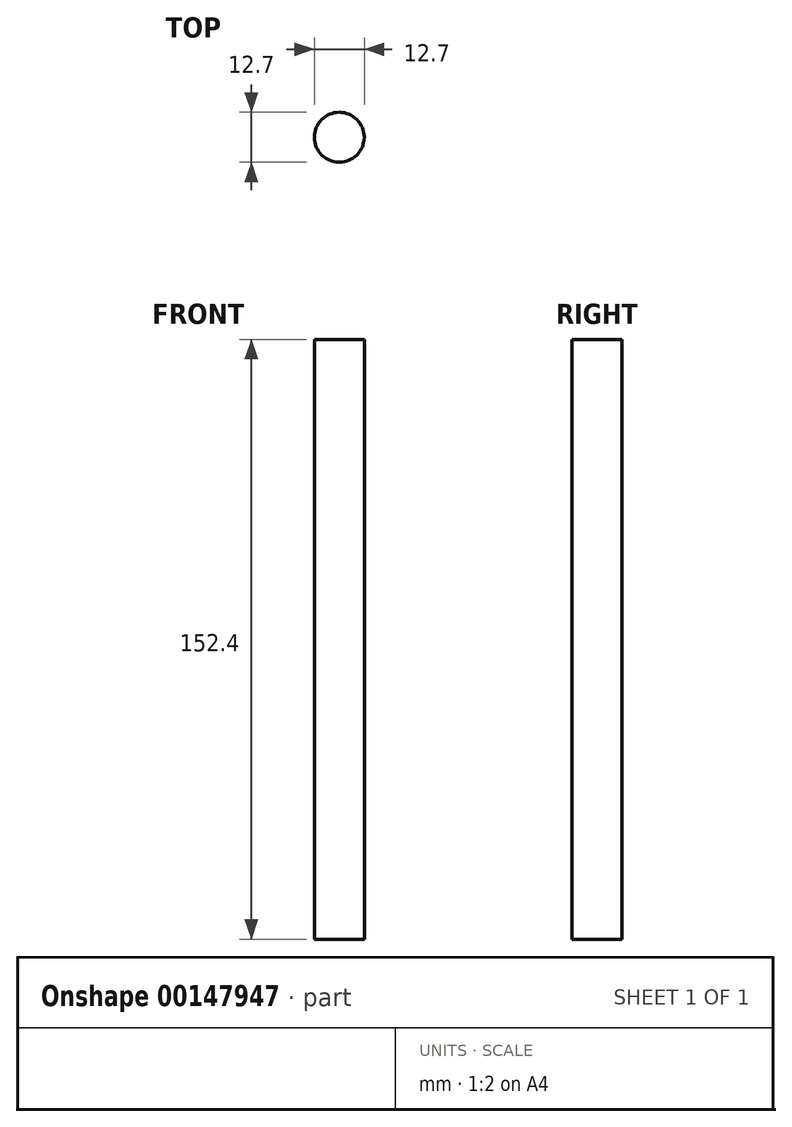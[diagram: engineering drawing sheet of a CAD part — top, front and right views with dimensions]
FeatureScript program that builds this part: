
annotation { "Feature Type Name" : "Feature", "Feature Type Description" : "" }
export const myFeature = defineFeature(function(context is Context, id is Id, definition is map)
    precondition{}
    {
        {
            var Q0;
            Q0=qCreatedBy(makeId("Top.planeOp"),FACE);
            var sketch = newSketch(context, id + "F0", { "sketchPlane" : qUnion([Q0])});
            skCircle(sketch, "E0", {"center": v(0, 0) * mm, "radius": 6.35 * mm});
            skSolve(sketch);
        }
        {
            var Q0;
            Q0=qSketchRegion(id+"F0",true);
            extrude(context, id + "F1", {"entities" : qUnion([Q0]), "depth" : 152.4 * mm});
        }
    });
